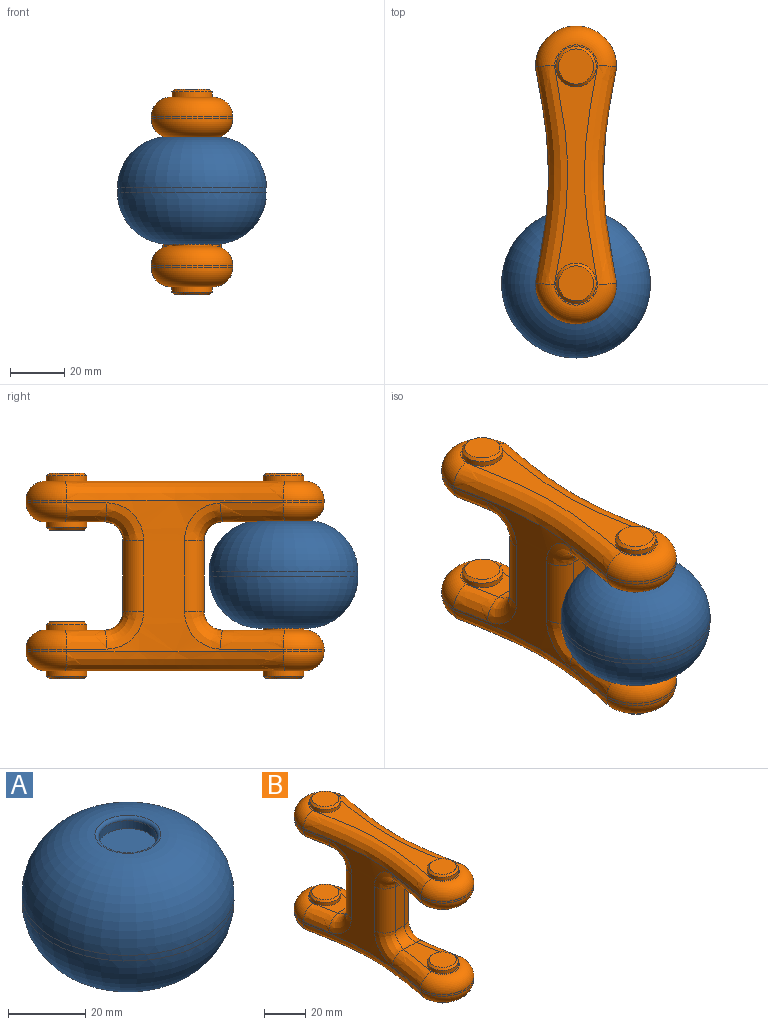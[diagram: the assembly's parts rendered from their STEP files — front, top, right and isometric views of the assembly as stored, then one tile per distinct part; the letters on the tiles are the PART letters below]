
ASSEMBLY  parts=2 mates=1
PART A: 9 faces, bbox 55x55x39.8 mm
  f0: cylinder r=27.5mm len=55mm, axis (0,0,-1), area 311mm2, adj f7,f8
  f1: cylinder r=7.55mm len=15.1mm, axis (0,0,-1), area 118.6mm2, adj f2,f6
  f2: plane 15.1x15.1mm, normal (0,0,-1), area 179.1mm2, adj f1
  f3: cylinder r=7.55mm len=15.1mm, axis (0,0,1), area 118.6mm2, adj f4,f5
  f4: plane 15.1x15.1mm, normal (0,0,1), area 179.1mm2, adj f3
  f5: torus R=8.55mm, axis (0,0,1), area 78.1mm2, adj f3,f8
  f6: torus R=8.55mm, axis (0,0,1), area 78.1mm2, adj f1,f7
  f7: torus R=8.5mm, axis (0,0,-1), area 3859.5mm2, adj f0,f6
  f8: torus R=8.5mm, axis (0,0,1), area 3859.5mm2, adj f0,f5
PART B: 74 faces, bbox 35.3x112.6x76 mm
  f0: cylinder r=15mm len=30mm, axis (0,0,-1), area 47.3mm2, adj f3,f5,f47,f58
  f1: cylinder r=15mm len=30mm, axis (0,0,-1), area 47.3mm2, adj f3,f5,f34,f61
  f2: cylinder r=15mm len=30mm, axis (0,0,-1), area 47.3mm2, adj f3,f5,f50,f62
  f3: extruded ~80x56mm, area 1140.8mm2, adj f0,f1,f2,f4,f38,f39,f41,f42
  f4: cylinder r=15mm len=30mm, axis (0,0,-1), area 47.3mm2, adj f3,f5,f35,f65
  f5: extruded ~80x56mm, area 1140.8mm2, adj f0,f1,f2,f4,f30,f31,f32,f33
  f6: plane 96.16x16.03mm, normal (0,0,1), area 619.8mm2, adj f26,f28,f62,f63,f64,f65
  f7: plane 96.16x16.03mm, normal (0,0,-1), area 619.8mm2, adj f22,f24,f58,f59,f60,f61
  f8: plane 26x6.12mm, normal (0,-1,0), area 159.1mm2, adj f32,f37,f40,f43
  f9: plane 30.37x15.99mm, normal (0,0,1), area 188.9mm2, adj f14,f30,f34,f37,f38
  f10: plane 30.37x15.99mm, normal (0,0,-1), area 188.9mm2, adj f16,f31,f35,f39,f40
  f11: plane 26x7.21mm, normal (0,1,0), area 187.4mm2, adj f45,f52,f53,f57
  f12: plane 21.8x15.97mm, normal (0,0,1), area 106.8mm2, adj f20,f44,f47,f51,f52
  f13: plane 21.8x15.97mm, normal (0,0,-1), area 106.8mm2, adj f18,f46,f50,f53,f54
  f14: cylinder r=7.5mm len=15mm, axis (0,0,-1), area 94.2mm2, adj f9,f69
  f15: plane 13x13mm, normal (0,0,1), area 132.7mm2, adj f69
  f16: cylinder r=7.5mm len=15mm, axis (0,0,1), area 94.2mm2, adj f10,f73
  f17: plane 13x13mm, normal (0,0,-1), area 132.7mm2, adj f73
  f18: cylinder r=7.5mm len=15mm, axis (0,0,1), area 94.2mm2, adj f13,f72
  f19: plane 13x13mm, normal (0,0,-1), area 132.7mm2, adj f72
  f20: cylinder r=7.5mm len=15mm, axis (0,0,-1), area 94.2mm2, adj f12,f68
  f21: plane 13x13mm, normal (0,0,1), area 132.7mm2, adj f68
  f22: cylinder r=7.5mm len=15mm, axis (0,0,1), area 94.2mm2, adj f7,f70
  f23: plane 13x13mm, normal (0,0,-1), area 132.7mm2, adj f70
  f24: cylinder r=7.5mm len=15mm, axis (0,0,1), area 94.2mm2, adj f7,f71
  f25: plane 13x13mm, normal (0,0,-1), area 132.7mm2, adj f71
  f26: cylinder r=7.5mm len=15mm, axis (0,0,-1), area 94.2mm2, adj f6,f67
  f27: plane 13x13mm, normal (0,0,1), area 132.7mm2, adj f67
  f28: cylinder r=7.5mm len=15mm, axis (0,0,-1), area 94.2mm2, adj f6,f66
  f29: plane 13x13mm, normal (0,0,1), area 132.7mm2, adj f66
  f30: bspline ~36.09x12.66mm, area 255.8mm2, adj f5,f9,f33,f34
  f31: bspline ~36.09x12.66mm, area 255.8mm2, adj f5,f10,f35,f36
  f32: cylinder r=7mm len=26mm, axis (0,0,-1), area 291.6mm2, adj f5,f8,f33,f36
  f33: bspline ~17.14x15.61mm, area 164.5mm2, adj f5,f30,f32,f37
  f34: torus R=8mm, axis (0,0,1), area 423.5mm2, adj f1,f9,f30,f38
  f35: torus R=8mm, axis (0,0,1), area 423.5mm2, adj f4,f10,f31,f39
  f36: bspline ~16.42x16.4mm, area 164.5mm2, adj f5,f31,f32,f40
  f37: cylinder r=7mm len=8.4mm, axis (-1,0,0), area 79.8mm2, adj f8,f9,f33,f41
  f38: bspline ~36.09x12.66mm, area 255.8mm2, adj f3,f9,f34,f41
  f39: bspline ~36.09x12.66mm, area 255.8mm2, adj f3,f10,f35,f42
  f40: cylinder r=7mm len=8.4mm, axis (1,0,0), area 79.8mm2, adj f8,f10,f36,f42
  f41: bspline ~16.4x14.64mm, area 164.5mm2, adj f3,f37,f38,f43
  f42: bspline ~17.14x15.61mm, area 164.5mm2, adj f3,f39,f40,f43
  f43: cylinder r=7mm len=26mm, axis (0,0,-1), area 291.6mm2, adj f3,f8,f41,f42
  f44: bspline ~29.75x11.79mm, area 162.4mm2, adj f5,f12,f47,f48
  f45: cylinder r=7mm len=26mm, axis (0,0,-1), area 302.8mm2, adj f5,f11,f48,f49
  f46: bspline ~29.75x11.79mm, area 162.4mm2, adj f5,f13,f49,f50
  f47: torus R=8mm, axis (0,0,1), area 423.5mm2, adj f0,f12,f44,f51
  f48: bspline ~16.66x16.47mm, area 168.9mm2, adj f5,f44,f45,f52
  f49: bspline ~17.13x15.8mm, area 168.9mm2, adj f5,f45,f46,f53
  f50: torus R=8mm, axis (0,0,1), area 423.5mm2, adj f2,f13,f46,f54
  f51: bspline ~29.75x11.79mm, area 162.4mm2, adj f3,f12,f47,f55
  f52: cylinder r=7mm len=10.87mm, axis (1,0,0), area 99.4mm2, adj f11,f12,f48,f55
  f53: cylinder r=7mm len=10.87mm, axis (-1,0,0), area 99.4mm2, adj f11,f13,f49,f56
  f54: bspline ~29.75x11.79mm, area 162.4mm2, adj f3,f13,f50,f56
  f55: bspline ~17.13x15.8mm, area 168.9mm2, adj f3,f51,f52,f57
  f56: bspline ~16.66x16.47mm, area 168.9mm2, adj f3,f53,f54,f57
  f57: cylinder r=7mm len=26mm, axis (0,0,-1), area 302.8mm2, adj f3,f11,f55,f56
  f58: torus R=8mm, axis (0,0,1), area 423.5mm2, adj f0,f7,f59,f60
  f59: bspline ~99.77x14.66mm, area 890.2mm2, adj f5,f7,f58,f61
  f60: bspline ~99.77x14.66mm, area 890.2mm2, adj f3,f7,f58,f61
  f61: torus R=8mm, axis (0,0,1), area 423.5mm2, adj f1,f7,f59,f60
  f62: torus R=8mm, axis (0,0,1), area 423.5mm2, adj f2,f6,f63,f64
  f63: bspline ~99.77x14.66mm, area 890.2mm2, adj f5,f6,f62,f65
  f64: bspline ~99.77x14.66mm, area 890.2mm2, adj f3,f6,f62,f65
  f65: torus R=8mm, axis (0,0,1), area 423.5mm2, adj f4,f6,f63,f64
  f66: cone r=6.5mm half-angle=45deg, axis (0,0,-1), area 62.2mm2, adj f28,f29
  f67: cone r=6.5mm half-angle=45deg, axis (0,0,-1), area 62.2mm2, adj f26,f27
  f68: cone r=6.5mm half-angle=45deg, axis (0,0,-1), area 62.2mm2, adj f20,f21
  f69: cone r=6.5mm half-angle=45deg, axis (0,0,-1), area 62.2mm2, adj f14,f15
  f70: cone r=6.5mm half-angle=45deg, axis (0,0,1), area 62.2mm2, adj f22,f23
  f71: cone r=6.5mm half-angle=45deg, axis (0,0,1), area 62.2mm2, adj f24,f25
  f72: cone r=6.5mm half-angle=45deg, axis (0,0,1), area 62.2mm2, adj f18,f19
  f73: cone r=6.5mm half-angle=45deg, axis (0,0,1), area 62.2mm2, adj f16,f17
PLACE A at identity
PLACE B t=(-68.01,-10.06,-15.7)mm
MATE fastened B.f1 <-> A.f0  axis (0,0,-1) through (-68.01,-54.42,36.3)mm
